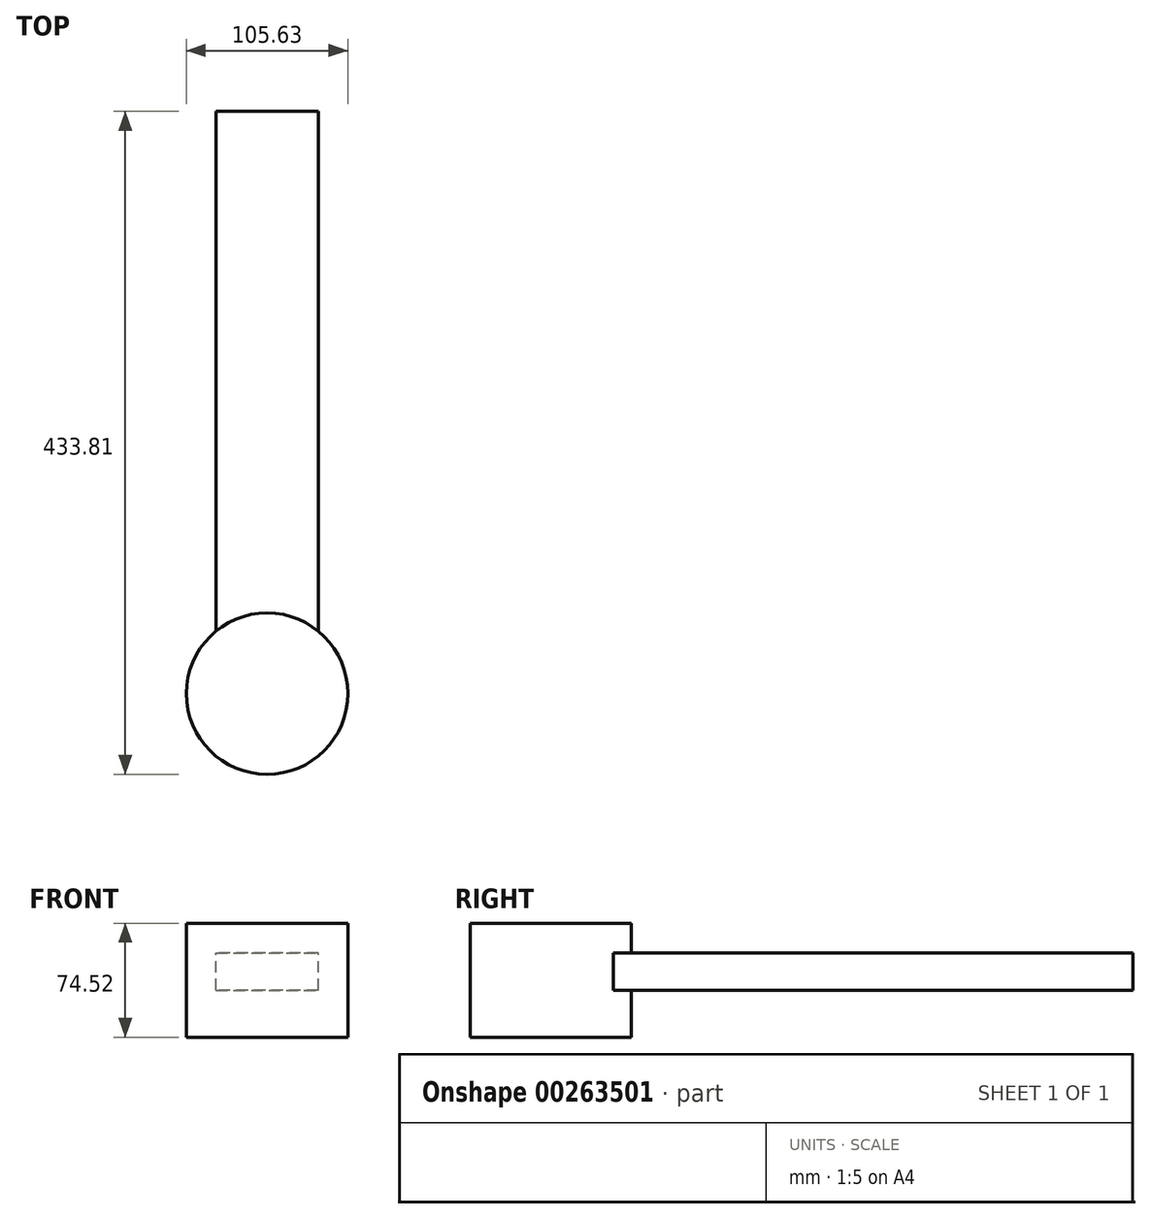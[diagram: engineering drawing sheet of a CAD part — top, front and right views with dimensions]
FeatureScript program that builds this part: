
annotation { "Feature Type Name" : "Feature", "Feature Type Description" : "" }
export const myFeature = defineFeature(function(context is Context, id is Id, definition is map)
    precondition{}
    {
        {
            var Q0;
            Q0=qCreatedBy(makeId("Front.planeOp"),FACE);
            var sketch = newSketch(context, id + "F0", { "sketchPlane" : qUnion([Q0])});
            skLineSegment(sketch, "E0.bottom", {"start": v(-17.1, 14.15) * mm, "end": v(49.7, 14.15) * mm});
            skLineSegment(sketch, "E0.top", {"start": v(-17.1, -10.3) * mm, "end": v(49.7, -10.3) * mm});
            skLineSegment(sketch, "E0.left", {"start": v(-17.1, 14.15) * mm, "end": v(-17.1, -10.3) * mm});
            skLineSegment(sketch, "E0.right", {"start": v(49.7, 14.15) * mm, "end": v(49.7, -10.3) * mm});
            skSolve(sketch);
        }
        {
            var Q0;
            Q0=makeQuery(id+"F0.imprint","IMPRINT",FACE,{"disambiguationData":[TD([[makeQuery(id+"F0.imprint","IMPRINT",EDGE,{"derivedFrom":sQuery(id+"F0.wireOp",EDGE,"E0.bottom")}),-1.0]])]});
            extrude(context, id + "F1", {"entities" : qUnion([Q0]), "depth" : 381 * mm});
        }
        {
            var Q0;
            Q0=makeQuery(id+"F1.opExtrude","CAP_FACE",FACE,{"disambiguationData":[OSD([sQuery(id+"F0.wireOp",EDGE,"E0.bottom"),sQuery(id+"F0.wireOp",EDGE,"E0.top"),sQuery(id+"F0.wireOp",EDGE,"E0.left"),sQuery(id+"F0.wireOp",EDGE,"E0.right")])],"isStart":false});
            var sketch = newSketch(context, id + "F2", { "sketchPlane" : qUnion([Q0])});
            skLineSegment(sketch, "E1", {"start": v(16.3, 14.15) * mm, "end": v(16.3, -10.3) * mm, "construction": true});
            skLineSegment(sketch, "E2.bottom", {"start": v(16.3, 33.45) * mm, "end": v(69.11, 33.45) * mm});
            skLineSegment(sketch, "E2.top", {"start": v(16.3, -41.07) * mm, "end": v(69.11, -41.07) * mm});
            skLineSegment(sketch, "E2.left", {"start": v(16.3, 33.45) * mm, "end": v(16.3, -41.07) * mm});
            skLineSegment(sketch, "E2.right", {"start": v(69.11, 33.45) * mm, "end": v(69.11, -41.07) * mm});
            skSolve(sketch);
        }
        {
            var Q0;
            Q0 = qSketchRegion(id + "F2", true);
            var Q1;
            Q1=sQuery(id+"F2.wireOp",EDGE,"E2.left");
            revolve(context, id + "F3", {"operationType" : NewBodyOperationType.ADD, "entities" : qUnion([Q0]), "axis" : qUnion([Q1]), "revolveType" : RevolveType.FULL});
        }
    });
